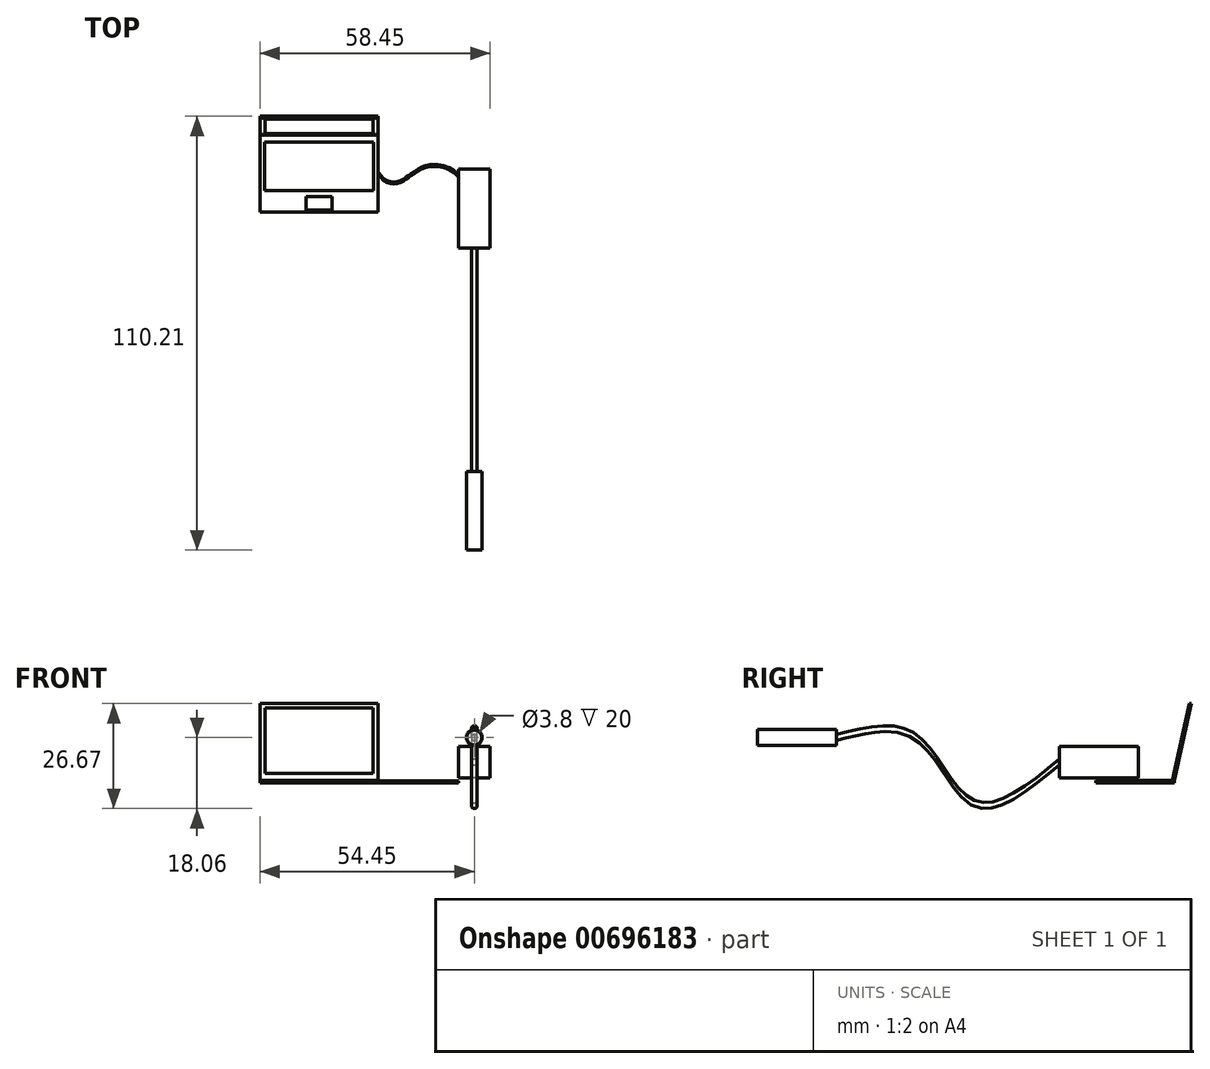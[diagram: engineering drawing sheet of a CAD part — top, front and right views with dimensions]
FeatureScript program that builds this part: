
annotation { "Feature Type Name" : "Feature", "Feature Type Description" : "" }
export const myFeature = defineFeature(function(context is Context, id is Id, definition is map)
    precondition{}
    {
        {
            var Q0;
            Q0=qCreatedBy(makeId("Front.planeOp"),FACE);
            var sketch = newSketch(context, id + "F0", { "sketchPlane" : qUnion([Q0])});
            skCircle(sketch, "E0", {"center": v(0, 0) * mm, "radius": 2 * mm});
            skCircle(sketch, "E1", {"center": v(0, 0) * mm, "radius": 1.9 * mm});
            skSolve(sketch);
        }
        {
            var Q0;
            Q0 = qSketchRegion(id + "F0", true);
            extrude(context, id + "F1", {"entities" : qUnion([Q0]), "depth" : 20 * mm, "offsetDistance" : 25 * mm});
        }
        {
            var Q0;
            Q0=makeQuery(id+"F0.imprint","IMPRINT",FACE,{"disambiguationData":[TD([[makeQuery(id+"F0.imprint","IMPRINT",EDGE,{"derivedFrom":sQuery(id+"F0.wireOp",EDGE,"E1")}),1.0]])]});
            extrude(context, id + "F2", {"entities" : qUnion([Q0]), "depth" : 20 * mm, "offsetDistance" : 25 * mm});
        }
        {
            var Q0;
            Q0=makeQuery(id+"F2.opExtrude","CAP_FACE",FACE,{"disambiguationData":[OSD([sQuery(id+"F0.wireOp",EDGE,"E1")])],"isStart":true});
            var sketch = newSketch(context, id + "F3", { "sketchPlane" : qUnion([Q0])});
            skCircle(sketch, "E2", {"center": v(0, 0) * mm, "radius": 0.75 * mm});
            skSolve(sketch);
        }
        {
            var Q0;
            Q0=qCreatedBy(makeId("Right.planeOp"),FACE);
            var sketch = newSketch(context, id + "F4", { "sketchPlane" : qUnion([Q0])});
            skFitSpline(sketch, "E3", {"points": [v(0, 0) * mm, v(20.4, 0) * mm, v(35.12, -16.82) * mm, v(56.75, -6.25) * mm], "startDerivative": vector(70.26, 18.29) * mm, "endDerivative": vector(68.74, 55.92) * mm});
            skSolve(sketch);
        }
        {
            var Q0;
            Q0=makeQuery(id+"F3.imprint","IMPRINT",FACE,{"disambiguationData":[TD([[makeQuery(id+"F3.imprint","IMPRINT",EDGE,{"derivedFrom":sQuery(id+"F3.wireOp",EDGE,"E2")}),1.0]])]});
            var Q1;
            Q1=sQuery(id+"F4.wireOp",EDGE,"E3");
            sweep(context, id + "F5", {"profiles" : qUnion([Q0]), "path" : qUnion([Q1]), "keepProfileOrientation" : true});
        }
        {
            var Q0;
            Q0=makeQuery(id+"F5.opSweep","CAP_FACE",FACE,{"disambiguationData":[OSD([sQuery(id+"F3.wireOp",EDGE,"E2"),sQuery(id+"F4.wireOp",VERTEX,"E3.end")])],"isStart":false});
            var sketch = newSketch(context, id + "F6", { "sketchPlane" : qUnion([Q0])});
            skLineSegment(sketch, "E4.bottom", {"start": v(-4, -2.25) * mm, "end": v(4, -2.25) * mm});
            skLineSegment(sketch, "E4.top", {"start": v(-4, -10.25) * mm, "end": v(4, -10.25) * mm});
            skLineSegment(sketch, "E4.left", {"start": v(-4, -2.25) * mm, "end": v(-4, -10.25) * mm});
            skLineSegment(sketch, "E4.right", {"start": v(4, -2.25) * mm, "end": v(4, -10.25) * mm});
            skPoint(sketch, "E4.middle", {"position": v(0, -6.25) * mm});
            skSolve(sketch);
        }
        {
            var Q0;
            Q0 = qSketchRegion(id + "F6", true);
            extrude(context, id + "F7", {"entities" : qUnion([Q0]), "depth" : 20 * mm, "offsetDistance" : 25 * mm});
        }
        {
            var Q0;
            Q0=makeQuery(id+"F7.opExtrude","SWEPT_FACE",FACE,{"disambiguationData":[OSD([sQuery(id+"F6.wireOp",EDGE,"E4.bottom")])]});
            cPlane(context, id + "F8", {"entities" : qUnion([Q0]), "cplaneType" : CPlaneType.OFFSET, "offset" : 9 * mm, "oppositeDirection" : true, "width" : 150 * mm, "height" : 150 * mm});
        }
        {
            var Q0;
            Q0=makeQuery(id+"F7.opExtrude","SWEPT_FACE",FACE,{"disambiguationData":[OSD([sQuery(id+"F6.wireOp",EDGE,"E4.right")])]});
            var sketch = newSketch(context, id + "F9", { "sketchPlane" : qUnion([Q0])});
            skLineSegment(sketch, "E5", {"start": v(-75.09, -2.25) * mm, "end": v(-75.09, -11.25) * mm});
            skCircle(sketch, "E6", {"center": v(-75.09, -11.25) * mm, "radius": 0.25 * mm});
            skSolve(sketch);
        }
        {
            var Q0;
            Q0=qCreatedBy(id+"F8.planeOp",FACE);
            var sketch = newSketch(context, id + "F10", { "sketchPlane" : qUnion([Q0])});
            skFitSpline(sketch, "E7", {"points": [v(-5, 75.1) * mm, v(-14.29, 77.07) * mm, v(-20.16, 73.5) * mm, v(-25.45, 75.94) * mm], "startDerivative": vector(-22.46, 23.73) * mm, "endDerivative": vector(-14.87, 26.24) * mm});
            skSolve(sketch);
        }
        {
            var Q0;
            Q0=makeQuery(id+"F9.imprint","IMPRINT",FACE,{"disambiguationData":[TD([[makeQuery(id+"F9.imprint","IMPRINT",EDGE,{"derivedFrom":sQuery(id+"F9.wireOp",EDGE,"E6")}),1.0]])]});
            var Q1;
            Q1=sQuery(id+"F10.wireOp",EDGE,"E7");
            sweep(context, id + "F11", {"profiles" : qUnion([Q0]), "path" : qUnion([Q1]), "keepProfileOrientation" : true});
        }
        {
            var Q0;
            Q0=makeQuery(id+"F11.opSweep","CAP_FACE",FACE,{"disambiguationData":[OSD([sQuery(id+"F9.wireOp",EDGE,"E6"),sQuery(id+"F10.wireOp",VERTEX,"E7.end")])],"isStart":false});
            var sketch = newSketch(context, id + "F12", { "sketchPlane" : qUnion([Q0])});
            skLineSegment(sketch, "E8.bottom", {"start": v(-65.94, -10.93) * mm, "end": v(-85.94, -10.93) * mm});
            skLineSegment(sketch, "E8.top", {"start": v(-65.94, -11.58) * mm, "end": v(-85.94, -11.58) * mm});
            skLineSegment(sketch, "E8.left", {"start": v(-65.94, -10.93) * mm, "end": v(-65.94, -11.58) * mm});
            skLineSegment(sketch, "E8.right", {"start": v(-85.94, -10.93) * mm, "end": v(-85.94, -11.58) * mm});
            skPoint(sketch, "E8.middle", {"position": v(-75.94, -11.25) * mm});
            skSolve(sketch);
        }
        {
            var Q0;
            Q0 = qSketchRegion(id + "F12", true);
            extrude(context, id + "F13", {"entities" : qUnion([Q0]), "depth" : 30 * mm, "offsetDistance" : 25 * mm});
        }
        {
            var Q0;
            Q0=makeQuery(id+"F13.opExtrude","CAP_FACE",FACE,{"disambiguationData":[OSD([sQuery(id+"F12.wireOp",EDGE,"E8.bottom"),sQuery(id+"F12.wireOp",EDGE,"E8.top"),sQuery(id+"F12.wireOp",EDGE,"E8.left"),sQuery(id+"F12.wireOp",EDGE,"E8.right")])],"isStart":true});
            var sketch = newSketch(context, id + "F14", { "sketchPlane" : qUnion([Q0])});
            skLineSegment(sketch, "E9", {"start": v(90.21, 8.61) * mm, "end": v(85.94, -10.93) * mm});
            skLineSegment(sketch, "E10", {"start": v(85.94, -10.93) * mm, "end": v(85.44, -10.93) * mm});
            skLineSegment(sketch, "E11", {"start": v(85.44, -10.93) * mm, "end": v(89.71, 8.61) * mm});
            skLineSegment(sketch, "E12", {"start": v(89.71, 8.61) * mm, "end": v(90.21, 8.61) * mm});
            skSolve(sketch);
        }
        {
            var Q0;
            Q0 = qSketchRegion(id + "F14", true);
            extrude(context, id + "F15", {"entities" : qUnion([Q0]), "operationType" : NewBodyOperationType.ADD, "oppositeDirection" : true, "depth" : 30 * mm, "offsetDistance" : 25 * mm});
        }
        {
            var Q0;
            Q0=makeQuery(id+"F15.opExtrude","SWEPT_FACE",FACE,{"disambiguationData":[OSD([sQuery(id+"F14.wireOp",EDGE,"E11")])]});
            var sketch = newSketch(context, id + "F16", { "sketchPlane" : qUnion([Q0])});
            skLineSegment(sketch, "E13.bottom", {"start": v(-25.74, 9.38) * mm, "end": v(-53.15, 9.38) * mm});
            skLineSegment(sketch, "E13.top", {"start": v(-25.74, 26.43) * mm, "end": v(-53.15, 26.43) * mm});
            skLineSegment(sketch, "E13.left", {"start": v(-25.74, 9.38) * mm, "end": v(-25.74, 26.43) * mm});
            skLineSegment(sketch, "E13.right", {"start": v(-53.15, 9.38) * mm, "end": v(-53.15, 26.43) * mm});
            skPoint(sketch, "E13.middle", {"position": v(-39.45, 17.9) * mm});
            skSolve(sketch);
        }
        {
            var Q0;
            Q0 = qSketchRegion(id + "F16", true);
            extrude(context, id + "F17", {"entities" : qUnion([Q0]), "depth" : 0.01 * mm, "offsetDistance" : 25 * mm});
        }
        {
            var Q0;
            Q0=makeQuery(id+"F13.opExtrude","SWEPT_FACE",FACE,{"disambiguationData":[OSD([sQuery(id+"F12.wireOp",EDGE,"E8.bottom")])]});
            var sketch = newSketch(context, id + "F18", { "sketchPlane" : qUnion([Q0])});
            skLineSegment(sketch, "E14.bottom", {"start": v(-25.56, 71.33) * mm, "end": v(-53.33, 71.33) * mm});
            skLineSegment(sketch, "E14.top", {"start": v(-25.56, 83.63) * mm, "end": v(-53.33, 83.63) * mm});
            skLineSegment(sketch, "E14.left", {"start": v(-25.56, 71.33) * mm, "end": v(-25.56, 83.63) * mm});
            skLineSegment(sketch, "E14.right", {"start": v(-53.33, 71.33) * mm, "end": v(-53.33, 83.63) * mm});
            skLineSegment(sketch, "E15.bottom", {"start": v(-36.17, 66.44) * mm, "end": v(-42.73, 66.44) * mm});
            skLineSegment(sketch, "E15.top", {"start": v(-36.17, 69.8) * mm, "end": v(-42.73, 69.8) * mm});
            skLineSegment(sketch, "E15.left", {"start": v(-36.17, 66.44) * mm, "end": v(-36.17, 69.8) * mm});
            skLineSegment(sketch, "E15.right", {"start": v(-42.73, 66.44) * mm, "end": v(-42.73, 69.8) * mm});
            skPoint(sketch, "E15.middle", {"position": v(-39.45, 68.12) * mm});
            skSolve(sketch);
        }
        {
            var Q0;
            Q0 = qSketchRegion(id + "F18", true);
            extrude(context, id + "F19", {"entities" : qUnion([Q0]), "depth" : 0.01 * mm, "offsetDistance" : 25 * mm});
        }
    });
